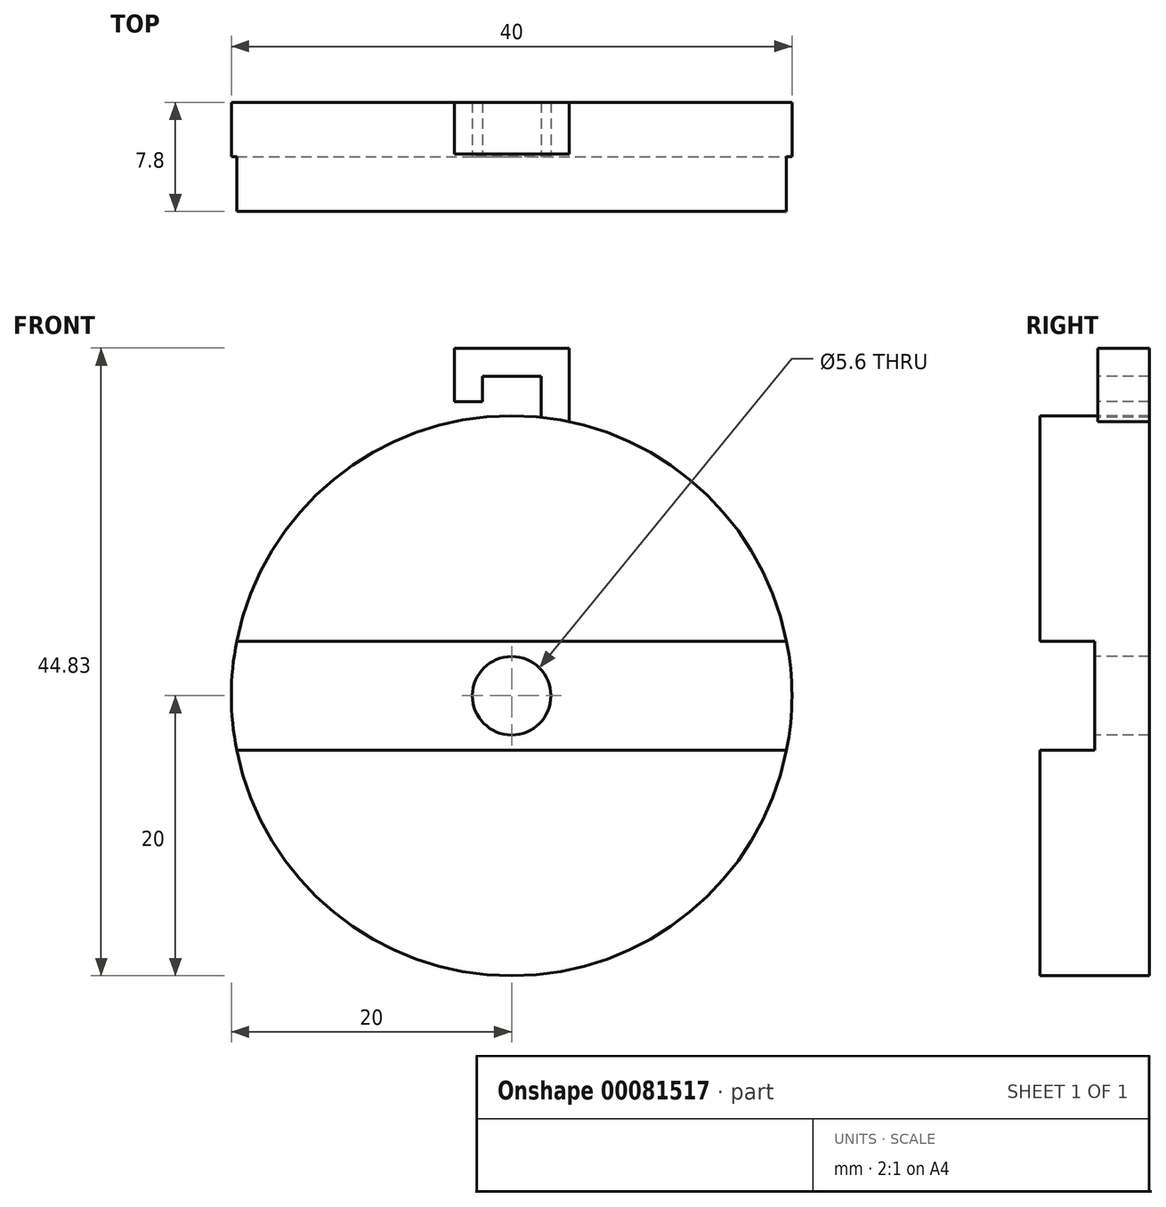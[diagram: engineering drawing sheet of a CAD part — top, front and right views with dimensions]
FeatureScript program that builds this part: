
annotation { "Feature Type Name" : "Feature", "Feature Type Description" : "" }
export const myFeature = defineFeature(function(context is Context, id is Id, definition is map)
    precondition{}
    {
        {
            var Q0;
            Q0=qCreatedBy(makeId("Front.planeOp"),FACE);
            var sketch = newSketch(context, id + "F0", { "sketchPlane" : qUnion([Q0])});
            skCircle(sketch, "E0", {"center": v(0, 0) * mm, "radius": 20 * mm});
            skSolve(sketch);
        }
        {
            var Q0;
            Q0 = qSketchRegion(id + "F0", true);
            var Q1;
            Q1=makeQuery(id+"F0.imprint","IMPRINT",FACE,{"disambiguationData":[TD([[makeQuery(id+"F0.imprint","IMPRINT",EDGE,{"derivedFrom":sQuery(id+"F0.wireOp",EDGE,"E0")}),1.0]])]});
            extrude(context, id + "F1", {"entities" : qUnion([Q0, Q1]), "oppositeDirection" : true, "depth" : 7.8 * mm});
        }
        {
            var Q0;
            Q0=makeQuery(id+"F1.opExtrude","CAP_FACE",FACE,{"disambiguationData":[OSD([sQuery(id+"F0.wireOp",EDGE,"E0")])],"isStart":true});
            var sketch = newSketch(context, id + "F2", { "sketchPlane" : qUnion([Q0])});
            skLineSegment(sketch, "E1.bottom", {"start": v(-20, 3.9) * mm, "end": v(20, 3.9) * mm});
            skLineSegment(sketch, "E1.top", {"start": v(-20, -3.9) * mm, "end": v(20, -3.9) * mm});
            skLineSegment(sketch, "E1.left", {"start": v(-20, 3.9) * mm, "end": v(-20, -3.9) * mm});
            skLineSegment(sketch, "E1.right", {"start": v(20, 3.9) * mm, "end": v(20, -3.9) * mm});
            skSolve(sketch);
        }
        {
            var Q0;
            {var subQ0=sQuery(id+"F2.wireOp",EDGE,"E1.bottom");var subQ1=makeQuery(id+"F1.opExtrude","CAP_EDGE",EDGE,{"disambiguationData":[OSD([sQuery(id+"F0.wireOp",EDGE,"E0")])],"isStart":true});var subQ4=makeQuery(id+"F2.imprint","INTERSECT",VERTEX,{"disambiguationData":[OD(0.0)],"derivedFrom":[subQ1,subQ0]});Q0=makeQuery(id+"F2.imprint","IMPRINT",FACE,{"disambiguationData":[TD([[makeQuery(id+"F2.imprint","IMPRINT",EDGE,{"disambiguationData":[TD([[subQ4,-1.0]])],"derivedFrom":subQ0}),-1.0]])]});}
            extrude(context, id + "F3", {"entities" : qUnion([Q0]), "operationType" : NewBodyOperationType.REMOVE, "oppositeDirection" : true, "depth" : 3.9 * mm});
        }
        {
            var Q0;
            Q0=makeQuery(id+"F3.boolean.opBoolean","COPY",FACE,{"derivedFrom":makeQuery(id+"F3.opExtrude","CAP_FACE",FACE,{"disambiguationData":[OSD([sQuery(id+"F0.wireOp",EDGE,"E0"),sQuery(id+"F2.wireOp",EDGE,"E1.bottom"),sQuery(id+"F2.wireOp",EDGE,"E1.top")])],"isStart":false})});
            var sketch = newSketch(context, id + "F4", { "sketchPlane" : qUnion([Q0])});
            skCircle(sketch, "E2", {"center": v(0, 0) * mm, "radius": 2.8 * mm});
            skSolve(sketch);
        }
        {
            var Q0;
            Q0 = qSketchRegion(id + "F4", true);
            extrude(context, id + "F5", {"entities" : qUnion([Q0]), "operationType" : NewBodyOperationType.REMOVE, "endBound" : BoundingType.THROUGH_ALL, "oppositeDirection" : true, "depth" : 25 * mm});
        }
        {
            var Q0;
            Q0=makeQuery(id+"F1.opExtrude","CAP_FACE",FACE,{"disambiguationData":[OSD([sQuery(id+"F0.wireOp",EDGE,"E0")])],"isStart":false});
            var sketch = newSketch(context, id + "F6", { "sketchPlane" : qUnion([Q0])});
            skLineSegment(sketch, "E3.bottom", {"start": v(-4.1, 24.83) * mm, "end": v(4.1, 24.83) * mm});
            skLineSegment(sketch, "E3.top", {"start": v(-4.1, 19.58) * mm, "end": v(4.1, 19.58) * mm});
            skLineSegment(sketch, "E3.left", {"start": v(-4.1, 24.83) * mm, "end": v(-4.1, 19.58) * mm});
            skLineSegment(sketch, "E3.right", {"start": v(4.1, 24.83) * mm, "end": v(4.1, 19.58) * mm});
            skSolve(sketch);
        }
        {
            var Q0;
            Q0 = qSketchRegion(id + "F6", true);
            extrude(context, id + "F7", {"entities" : qUnion([Q0]), "operationType" : NewBodyOperationType.ADD, "oppositeDirection" : true, "depth" : 3.7 * mm});
        }
        {
            var Q0;
            Q0=makeQuery(id+"F7.opExtrude","CAP_FACE",FACE,{"disambiguationData":[OSD([sQuery(id+"F6.wireOp",EDGE,"E3.bottom"),sQuery(id+"F6.wireOp",EDGE,"E3.top"),sQuery(id+"F6.wireOp",EDGE,"E3.left"),sQuery(id+"F6.wireOp",EDGE,"E3.right")])],"isStart":false});
            var sketch = newSketch(context, id + "F8", { "sketchPlane" : qUnion([Q0])});
            skLineSegment(sketch, "E4", {"start": v(-2.1, 22.2) * mm, "end": v(-2.1, 22.83) * mm});
            skLineSegment(sketch, "E5", {"start": v(-2.1, 22.83) * mm, "end": v(2.1, 22.83) * mm});
            skLineSegment(sketch, "E6", {"start": v(2.1, 22.83) * mm, "end": v(2.1, 19.89) * mm});
            skLineSegment(sketch, "E7.top", {"start": v(-4.1, 21) * mm, "end": v(-2.1, 21) * mm});
            skLineSegment(sketch, "E7.right", {"start": v(-2.1, 22.2) * mm, "end": v(-2.1, 21) * mm});
            skPoint(sketch, "E7.left.start.orphan", {"position": v(-4.1, 22.2) * mm});
            skLineSegment(sketch, "E8", {"start": v(-4.1, 21) * mm, "end": v(-4.1, 19.58) * mm});
            skArc(sketch, "E9", {"start": v(2.1, 19.89) * mm, "mid": v(-1.01, 19.97) * mm, "end": v(-4.1, 19.58) * mm});
            skSolve(sketch);
        }
        {
            var Q0;
            Q0 = qSketchRegion(id + "F8", true);
            extrude(context, id + "F9", {"entities" : qUnion([Q0]), "operationType" : NewBodyOperationType.REMOVE, "endBound" : BoundingType.THROUGH_ALL, "oppositeDirection" : true, "depth" : 25 * mm});
        }
    });
